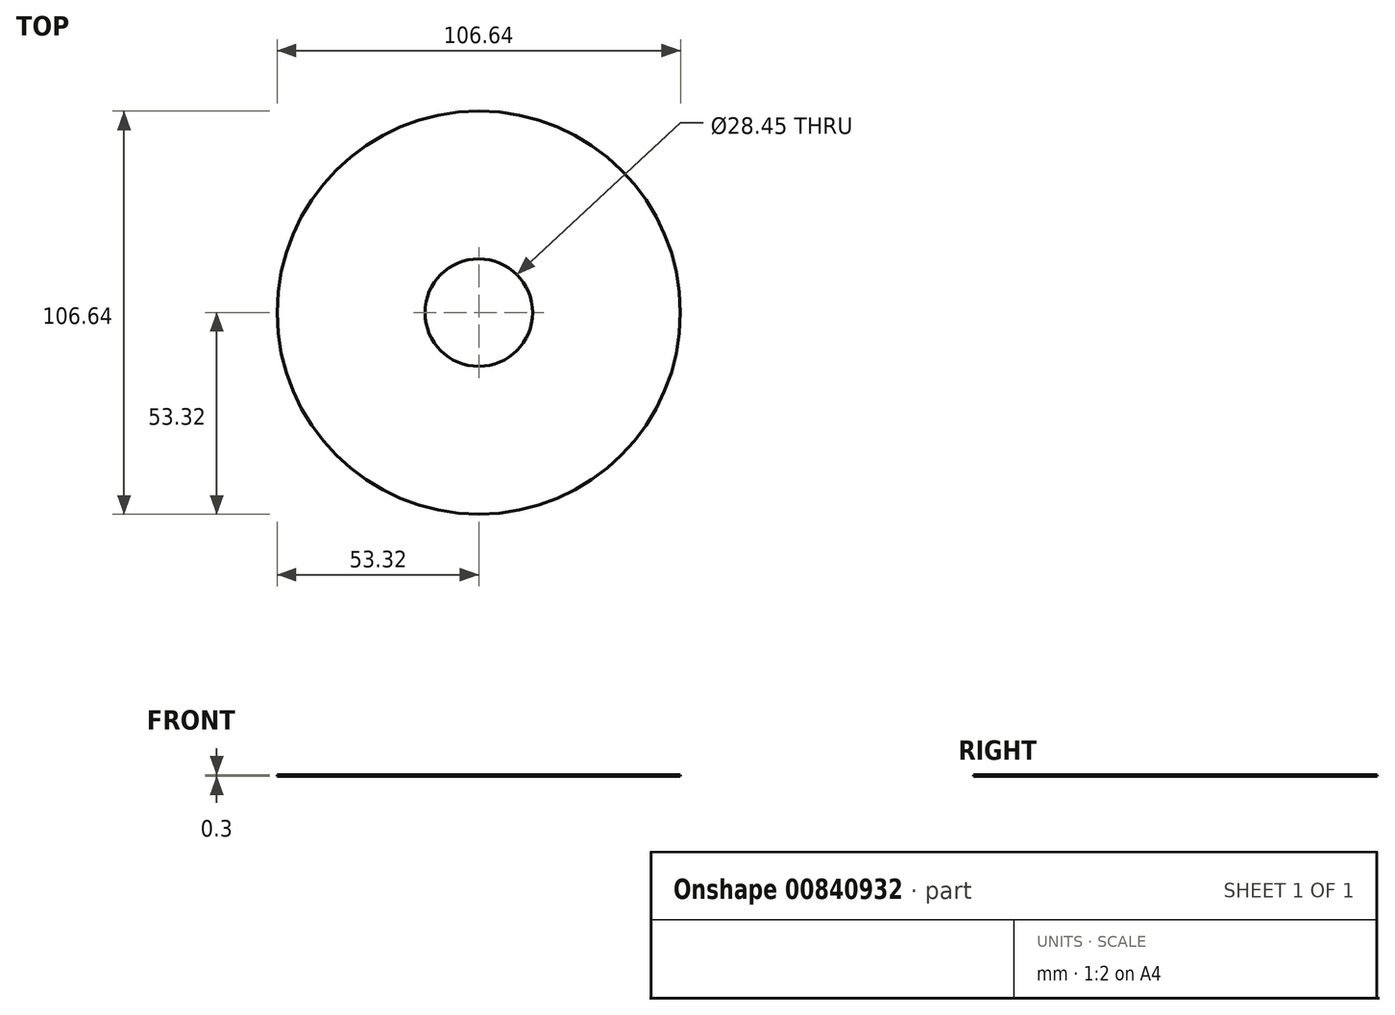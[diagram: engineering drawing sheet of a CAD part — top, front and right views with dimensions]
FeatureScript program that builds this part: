
annotation { "Feature Type Name" : "Feature", "Feature Type Description" : "" }
export const myFeature = defineFeature(function(context is Context, id is Id, definition is map)
    precondition{}
    {
        {
            var Q0;
            Q0=qCreatedBy(makeId("Top.planeOp"),FACE);
            var sketch = newSketch(context, id + "F0", { "sketchPlane" : qUnion([Q0])});
            skCircle(sketch, "E0", {"center": v(0, 0) * mm, "radius": 53.32 * mm});
            skCircle(sketch, "E1", {"center": v(0, 0) * mm, "radius": 50.32 * mm});
            skCircle(sketch, "E2", {"center": v(0, 0) * mm, "radius": 14.22 * mm});
            skSolve(sketch);
        }
        {
            var Q0;
            Q0=makeQuery(id+"F0.imprint","IMPRINT",FACE,{"disambiguationData":[TD([[makeQuery(id+"F0.imprint","IMPRINT",EDGE,{"derivedFrom":sQuery(id+"F0.wireOp",EDGE,"E1")}),1.0]])]});
            var Q1;
            Q1=makeQuery(id+"F0.imprint","IMPRINT",FACE,{"disambiguationData":[TD([[makeQuery(id+"F0.imprint","IMPRINT",EDGE,{"derivedFrom":sQuery(id+"F0.wireOp",EDGE,"E0")}),1.0]])]});
            extrude(context, id + "F1", {"entities" : qUnion([Q0, Q1]), "depth" : 0.3 * mm, "offsetDistance" : 25 * mm});
        }
    });
